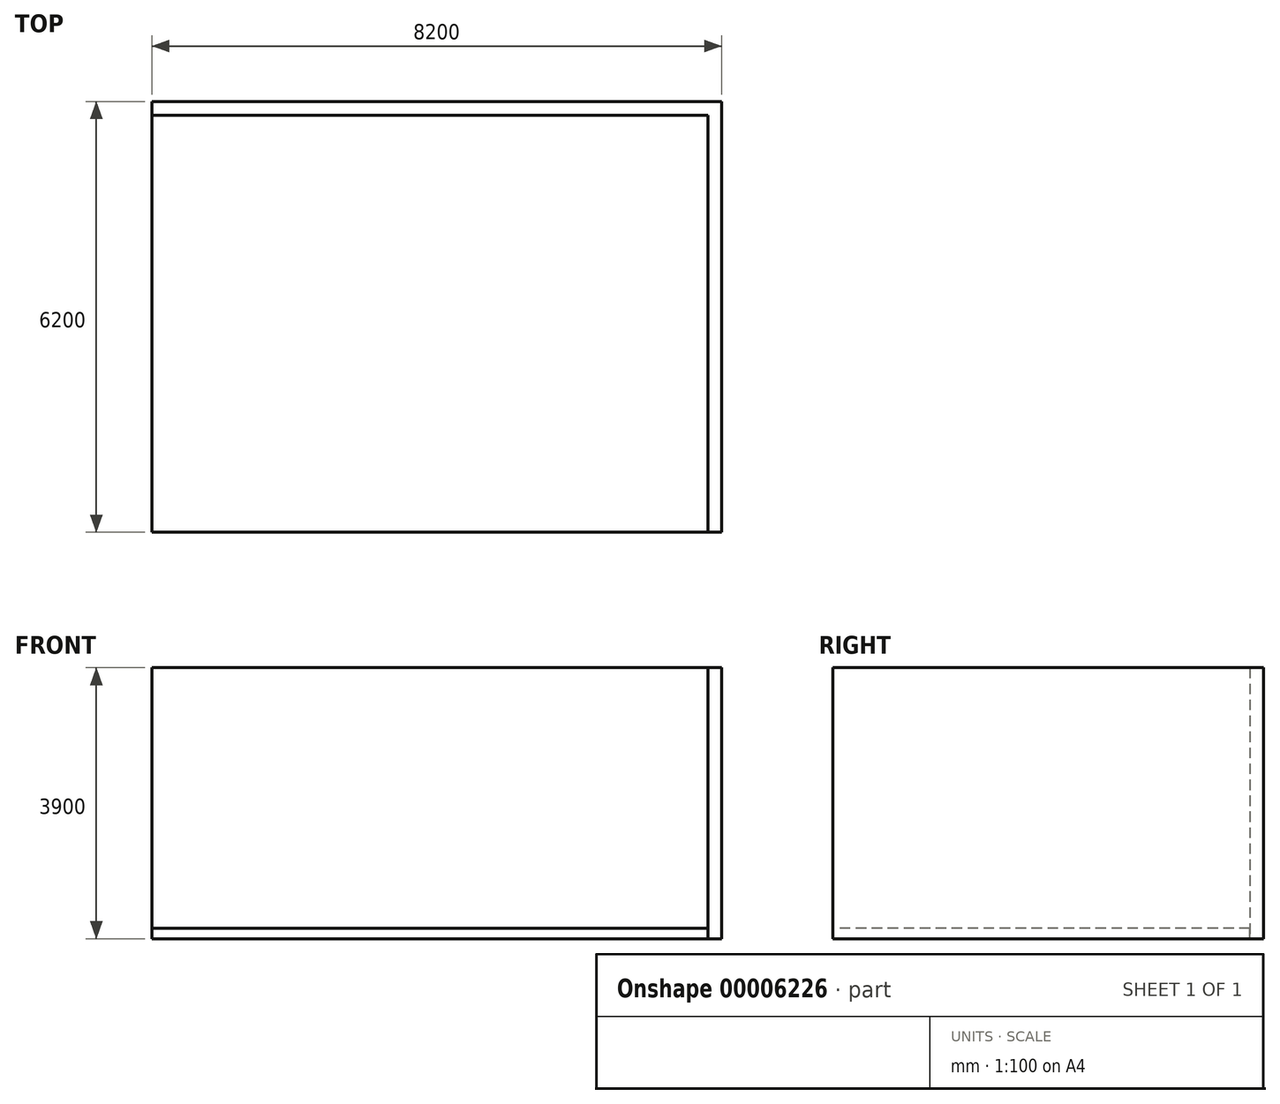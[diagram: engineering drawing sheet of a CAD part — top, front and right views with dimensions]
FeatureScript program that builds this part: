
annotation { "Feature Type Name" : "Feature", "Feature Type Description" : "" }
export const myFeature = defineFeature(function(context is Context, id is Id, definition is map)
    precondition{}
    {
        {
            var Q0;
            Q0=qCreatedBy(makeId("Top.planeOp"),FACE);
            var sketch = newSketch(context, id + "F0", { "sketchPlane" : qUnion([Q0])});
            skLineSegment(sketch, "E0.rect.bottom", {"start": v(4000, 3000) * mm, "end": v(-4000, 3000) * mm});
            skLineSegment(sketch, "E0.rect.top", {"start": v(4000, -3000) * mm, "end": v(-4000, -3000) * mm});
            skLineSegment(sketch, "E0.rect.left", {"start": v(4000, 3000) * mm, "end": v(4000, -3000) * mm});
            skLineSegment(sketch, "E0.rect.right", {"start": v(-4000, 3000) * mm, "end": v(-4000, -3000) * mm});
            skPoint(sketch, "E0.rect.middle", {"position": v(0, 0) * mm});
            skSolve(sketch);
        }
        {
            var Q0;
            Q0=makeQuery(id+"F0.imprint","IMPRINT",FACE,{"disambiguationData":[TD([[makeQuery(id+"F0.imprint","IMPRINT",EDGE,{"derivedFrom":sQuery(id+"F0.wireOp",EDGE,"E0.rect.bottom")}),1.0]])]});
            extrude(context, id + "F1", {"entities" : qUnion([Q0]), "oppositeDirection" : true, "depth" : 150 * mm});
        }
        {
            var Q0;
            Q0=makeQuery(id+"F1.opExtrude","CAP_FACE",FACE,{"disambiguationData":[OSD([sQuery(id+"F0.wireOp",EDGE,"E0.rect.bottom"),sQuery(id+"F0.wireOp",EDGE,"E0.rect.top"),sQuery(id+"F0.wireOp",EDGE,"E0.rect.left"),sQuery(id+"F0.wireOp",EDGE,"E0.rect.right")])],"isStart":false});
            var sketch = newSketch(context, id + "F2", { "sketchPlane" : qUnion([Q0])});
            skLineSegment(sketch, "E1.bottom", {"start": v(-4000, -3000) * mm, "end": v(4000, -3000) * mm});
            skLineSegment(sketch, "E1.top", {"start": v(-4000, -3200) * mm, "end": v(4000, -3200) * mm});
            skLineSegment(sketch, "E1.left", {"start": v(-4000, -3000) * mm, "end": v(-4000, -3200) * mm});
            skLineSegment(sketch, "E2.bottom", {"start": v(4000, 3000) * mm, "end": v(4200, 3000) * mm});
            skLineSegment(sketch, "E2.top", {"start": v(4000, -3200) * mm, "end": v(4200, -3200) * mm});
            skLineSegment(sketch, "E2.left", {"start": v(4000, 3000) * mm, "end": v(4000, -3000) * mm});
            skLineSegment(sketch, "E2.right", {"start": v(4200, 3000) * mm, "end": v(4200, -3200) * mm});
            skSolve(sketch);
        }
        {
            var Q0;
            Q0=makeQuery(id+"F2.imprint","IMPRINT",FACE,{"disambiguationData":[TD([[makeQuery(id+"F2.imprint","IMPRINT",EDGE,{"derivedFrom":sQuery(id+"F2.wireOp",EDGE,"E1.bottom")}),1.0]])]});
            extrude(context, id + "F3", {"entities" : qUnion([Q0]), "oppositeDirection" : true, "depth" : 3900 * mm});
        }
    });
